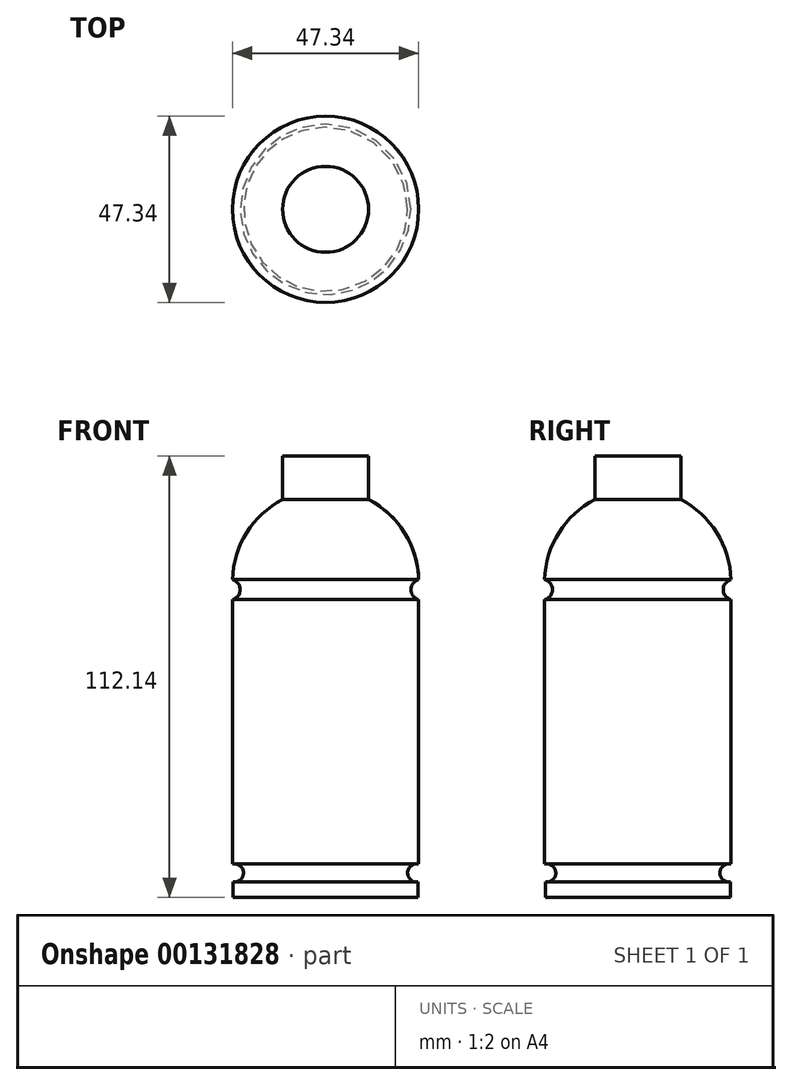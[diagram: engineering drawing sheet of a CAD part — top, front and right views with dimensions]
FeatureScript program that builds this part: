
annotation { "Feature Type Name" : "Feature", "Feature Type Description" : "" }
export const myFeature = defineFeature(function(context is Context, id is Id, definition is map)
    precondition{}
    {
        {
            var Q0;
            Q0=qCreatedBy(makeId("Front.planeOp"),FACE);
            var sketch = newSketch(context, id + "F0", { "sketchPlane" : qUnion([Q0])});
            skLineSegment(sketch, "E0", {"start": v(0, 56.38) * mm, "end": v(10.92, 56.38) * mm});
            skLineSegment(sketch, "E1", {"start": v(10.92, 56.38) * mm, "end": v(10.92, 45.32) * mm});
            skArc(sketch, "E2", {"start": v(23.67, 24.97) * mm, "mid": v(20.06, 36.88) * mm, "end": v(10.92, 45.32) * mm});
            skArc(sketch, "E3", {"start": v(23.67, 24.97) * mm, "mid": v(21.68, 22.42) * mm, "end": v(23.67, 19.88) * mm});
            skLineSegment(sketch, "E4", {"start": v(23.67, 19.88) * mm, "end": v(23.67, -47.28) * mm});
            skPoint(sketch, "E5", {"position": v(23.52, -51.89) * mm});
            skArc(sketch, "E6", {"start": v(23.67, -47.28) * mm, "mid": v(20.85, -49.5) * mm, "end": v(23.52, -51.89) * mm});
            skLineSegment(sketch, "E7", {"start": v(23.52, -51.89) * mm, "end": v(23.52, -55.76) * mm});
            skLineSegment(sketch, "E8", {"start": v(23.52, -55.76) * mm, "end": v(0, -55.76) * mm});
            skLineSegment(sketch, "E9", {"start": v(0, 56.38) * mm, "end": v(0, -55.76) * mm});
            skSolve(sketch);
        }
        {
            var Q0;
            Q0=makeQuery(id+"F0.imprint","IMPRINT",FACE,{"disambiguationData":[TD([[makeQuery(id+"F0.imprint","IMPRINT",EDGE,{"derivedFrom":sQuery(id+"F0.wireOp",EDGE,"E0")}),-1.0]])]});
            var Q1;
            Q1=sQuery(id+"F0.wireOp",EDGE,"E9");
            revolve(context, id + "F1", {"entities" : qUnion([Q0]), "axis" : qUnion([Q1]), "revolveType" : RevolveType.FULL});
        }
    });
